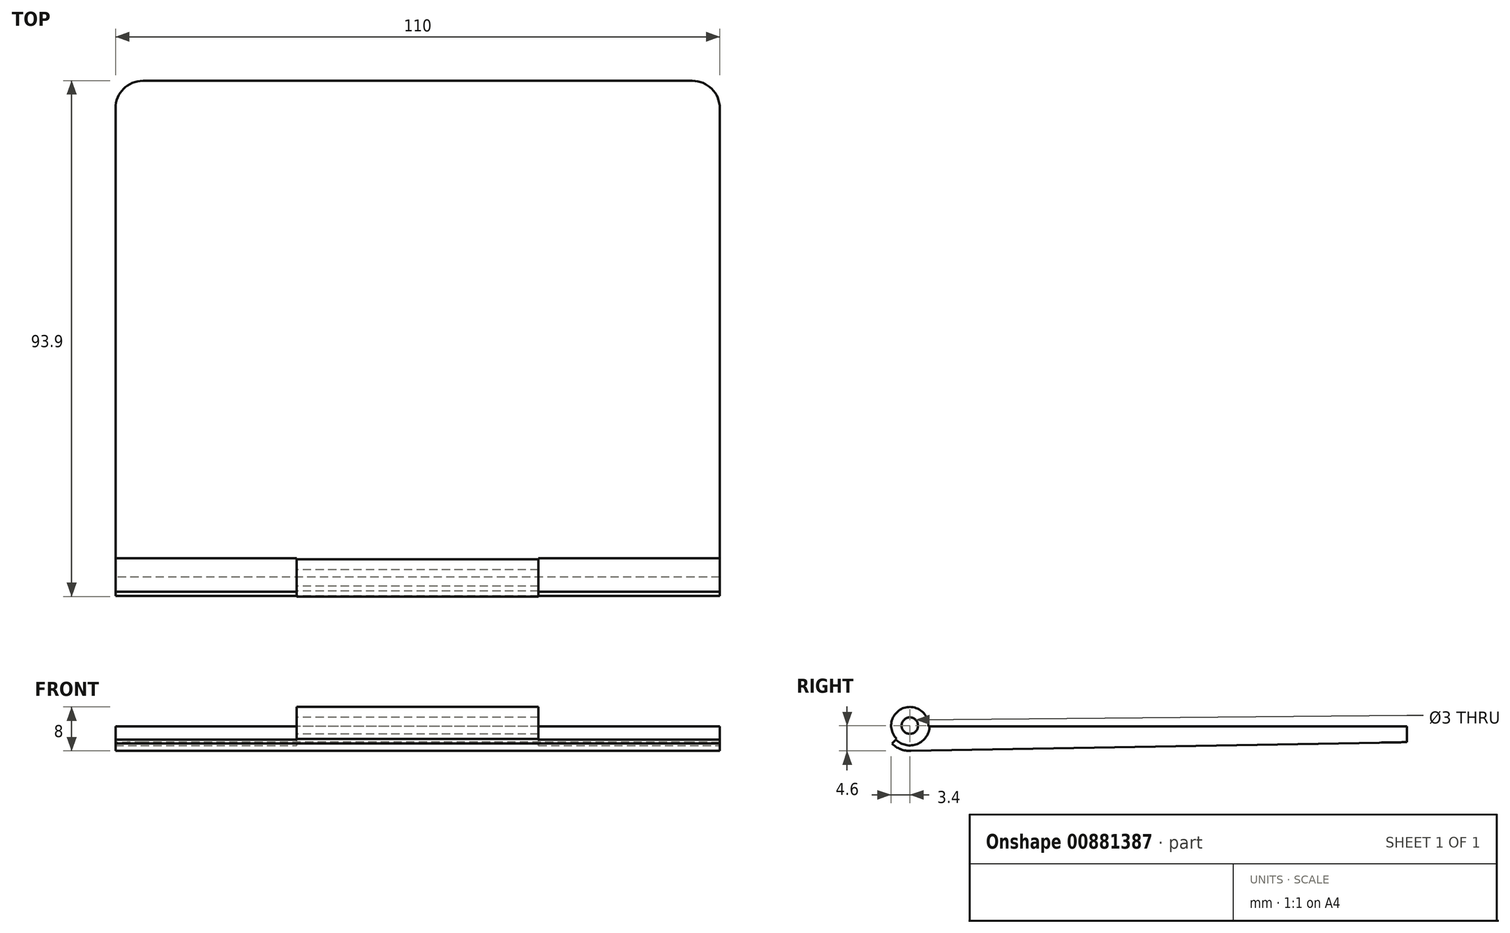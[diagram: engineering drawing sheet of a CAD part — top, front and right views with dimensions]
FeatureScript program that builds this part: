
annotation { "Feature Type Name" : "Feature", "Feature Type Description" : "" }
export const myFeature = defineFeature(function(context is Context, id is Id, definition is map)
    precondition{}
    {
        {
            var Q0;
            Q0=qCreatedBy(makeId("Top.planeOp"),FACE);
            var sketch = newSketch(context, id + "F0", { "sketchPlane" : qUnion([Q0])});
            skLineSegment(sketch, "E0.bottom", {"start": v(55, -45) * mm, "end": v(-55, -45) * mm});
            skLineSegment(sketch, "E0.top", {"start": v(55, 45) * mm, "end": v(-55, 45) * mm});
            skLineSegment(sketch, "E0.left", {"start": v(55, -45) * mm, "end": v(55, 45) * mm});
            skLineSegment(sketch, "E0.right", {"start": v(-55, -45) * mm, "end": v(-55, 45) * mm});
            skPoint(sketch, "E0.middle", {"position": v(0, 0) * mm});
            skLineSegment(sketch, "E1.bottom", {"start": v(52, 42) * mm, "end": v(-52, 42) * mm, "construction": true});
            skLineSegment(sketch, "E1.top", {"start": v(52, -42) * mm, "end": v(-52, -42) * mm, "construction": true});
            skLineSegment(sketch, "E1.left", {"start": v(52, 42) * mm, "end": v(52, -42) * mm, "construction": true});
            skLineSegment(sketch, "E1.right", {"start": v(-52, 42) * mm, "end": v(-52, -42) * mm, "construction": true});
            skSolve(sketch);
        }
        {
            var Q0;
            Q0=makeQuery(id+"F0.imprint","IMPRINT",FACE,{"disambiguationData":[TD([[makeQuery(id+"F0.imprint","IMPRINT",EDGE,{"derivedFrom":sQuery(id+"F0.wireOp",EDGE,"E0.bottom")}),-1.0]])]});
            extrude(context, id + "F1", {"entities" : qUnion([Q0]), "depth" : 3 * mm, "offsetDistance" : 25 * mm});
        }
        {
            var Q0;
            Q0=qCreatedBy(makeId("Right.planeOp"),FACE);
            var sketch = newSketch(context, id + "F2", { "sketchPlane" : qUnion([Q0])});
            skLineSegment(sketch, "E2", {"start": v(-42, 6.82) * mm, "end": v(-42, -5.48) * mm, "construction": true});
            skCircle(sketch, "E3", {"center": v(-45.5, 3) * mm, "radius": 1.5 * mm});
            skCircle(sketch, "E4", {"center": v(-45.5, 3) * mm, "radius": 3.4 * mm});
            skPoint(sketch, "E5", {"position": v(-42.1, 3) * mm});
            skPoint(sketch, "E6", {"position": v(-45.5, -0.4) * mm});
            skLineSegment(sketch, "E7", {"start": v(-48.55, 3) * mm, "end": v(-31.88, 3) * mm, "construction": true});
            skPoint(sketch, "E8", {"position": v(-42, 3) * mm});
            skCircle(sketch, "E9", {"center": v(-45.5, 3) * mm, "radius": 3.6 * mm});
            skLineSegment(sketch, "E10", {"start": v(-45.5, 3) * mm, "end": v(-49.84, -1.34) * mm, "construction": true});
            skPoint(sketch, "E11", {"position": v(-48.05, 0.45) * mm});
            skArc(sketch, "E12", {"start": v(-48.75, -0.25) * mm, "mid": v(-45.32, -1.6) * mm, "end": v(-42, 0.02) * mm});
            skPoint(sketch, "E13", {"position": v(-48.75, -0.25) * mm});
            skPoint(sketch, "E14", {"position": v(-42, 0.02) * mm});
            skLineSegment(sketch, "E15", {"start": v(-48.75, -0.25) * mm, "end": v(-48.05, 0.45) * mm});
            skPoint(sketch, "E16", {"position": v(-43.51, 0) * mm});
            skLineSegment(sketch, "E17", {"start": v(-42, 0.02) * mm, "end": v(-43.51, 0) * mm});
            skLineSegment(sketch, "E18", {"start": v(-42.1, 3) * mm, "end": v(-41.9, 3) * mm});
            skLineSegment(sketch, "E19", {"start": v(-48.05, 0.45) * mm, "end": v(-47.9, 0.6) * mm});
            skLineSegment(sketch, "E20", {"start": v(-43.51, 0) * mm, "end": v(-43.9, 0) * mm});
            skSolve(sketch);
        }
        {
            var Q0;
            Q0=makeQuery(id+"F2.imprint","IMPRINT",FACE,{"disambiguationData":[TD([[makeQuery(id+"F2.imprint","IMPRINT",EDGE,{"derivedFrom":sQuery(id+"F2.wireOp",EDGE,"E3")}),-1.0]])]});
            var Q1;
            Q1=makeQuery(id+"F2.imprint","IMPRINT",FACE,{"disambiguationData":[TD([[makeQuery(id+"F2.imprint","IMPRINT",EDGE,{"derivedFrom":sQuery(id+"F2.wireOp",EDGE,"E4")}),-1.0]])]});
            var Q2;
            Q2=makeQuery(id+"F2.imprint","IMPRINT",FACE,{"disambiguationData":[TD([[makeQuery(id+"F2.imprint","IMPRINT",EDGE,{"derivedFrom":sQuery(id+"F2.wireOp",EDGE,"E3")}),1.0]])]});
            var Q3;
            Q3=makeQuery(id+"F1.opExtrude","SWEPT_FACE",FACE,{"disambiguationData":[OSD([sQuery(id+"F0.wireOp",EDGE,"E0.right")])]});
            var Q4;
            Q4=makeQuery(id+"F1.opExtrude","SWEPT_FACE",FACE,{"disambiguationData":[OSD([sQuery(id+"F0.wireOp",EDGE,"E0.left")])]});
            extrude(context, id + "F3", {"entities" : qUnion([Q0, Q1, Q2]), "operationType" : NewBodyOperationType.REMOVE, "endBound" : BoundingType.UP_TO_SURFACE, "oppositeDirection" : true, "depth" : 25 * mm, "endBoundEntityFace" : qUnion([Q3]), "offsetDistance" : 25 * mm, "hasSecondDirection" : true, "secondDirectionBound" : SecondDirectionBoundingType.UP_TO_SURFACE, "secondDirectionOppositeDirection" : false, "secondDirectionDepth" : 25 * mm, "secondDirectionBoundEntityFace" : qUnion([Q4])});
        }
        {
            var Q0;
            {var subQ0=sQuery(id+"F2.wireOp",EDGE,"E18");Q0=makeQuery(id+"F2.imprint","IMPRINT",FACE,{"disambiguationData":[TD([[makeQuery(id+"F2.imprint","IMPRINT",EDGE,{"derivedFrom":subQ0}),-1.0]])]});}
            var Q1;
            {var subQ0=sQuery(id+"F2.wireOp",EDGE,"E19");Q1=makeQuery(id+"F2.imprint","IMPRINT",FACE,{"disambiguationData":[TD([[makeQuery(id+"F2.imprint","IMPRINT",EDGE,{"derivedFrom":subQ0}),-1.0]])]});}
            var Q2;
            Q2=makeQuery(id+"F2.imprint","IMPRINT",FACE,{"disambiguationData":[TD([[makeQuery(id+"F2.imprint","IMPRINT",EDGE,{"derivedFrom":sQuery(id+"F2.wireOp",EDGE,"E3")}),-1.0]])]});
            extrude(context, id + "F4", {"entities" : qUnion([Q0, Q1, Q2]), "operationType" : NewBodyOperationType.ADD, "depth" : 22 * mm, "offsetDistance" : 25 * mm, "hasSecondDirection" : true, "secondDirectionOppositeDirection" : true, "secondDirectionDepth" : 22 * mm});
        }
        {
            var Q0;
            Q0=makeQuery(id+"F2.imprint","IMPRINT",FACE,{"disambiguationData":[TD([[makeQuery(id+"F2.imprint","IMPRINT",EDGE,{"derivedFrom":sQuery(id+"F2.wireOp",EDGE,"E12")}),1.0]])]});
            var Q1;
            Q1=makeQuery(id+"F1.opExtrude","SWEPT_FACE",FACE,{"disambiguationData":[OSD([sQuery(id+"F0.wireOp",EDGE,"E0.left")])]});
            var Q2;
            Q2=makeQuery(id+"F1.opExtrude","SWEPT_FACE",FACE,{"disambiguationData":[OSD([sQuery(id+"F0.wireOp",EDGE,"E0.right")])]});
            extrude(context, id + "F5", {"entities" : qUnion([Q0]), "operationType" : NewBodyOperationType.ADD, "endBound" : BoundingType.UP_TO_SURFACE, "depth" : 25 * mm, "endBoundEntityFace" : qUnion([Q1]), "offsetDistance" : 25 * mm, "hasSecondDirection" : true, "secondDirectionBound" : SecondDirectionBoundingType.UP_TO_SURFACE, "secondDirectionOppositeDirection" : true, "secondDirectionDepth" : 25 * mm, "secondDirectionBoundEntityFace" : qUnion([Q2])});
        }
        {
            var Q0;
            Q0=makeQuery(id+"F4.boolean.opBoolean","MERGE",FACE,{"derivedFrom":[makeQuery(id+"F1.opExtrude","CAP_FACE",FACE,{"disambiguationData":[OSD([sQuery(id+"F0.wireOp",EDGE,"E0.bottom"),sQuery(id+"F0.wireOp",EDGE,"E0.top"),sQuery(id+"F0.wireOp",EDGE,"E0.left"),sQuery(id+"F0.wireOp",EDGE,"E0.right")])],"isStart":false}),makeQuery(id+"F4.opExtrude","SWEPT_FACE",FACE,{"disambiguationData":[OSD([sQuery(id+"F2.wireOp",EDGE,"E18")])]})]});
            var sketch = newSketch(context, id + "F6", { "sketchPlane" : qUnion([Q0])});
            skLineSegment(sketch, "E21.bottom", {"start": v(-55, 45) * mm, "end": v(55, 45) * mm});
            skLineSegment(sketch, "E21.top", {"start": v(-55, -41.9) * mm, "end": v(-22, -41.9) * mm});
            skLineSegment(sketch, "E21.left", {"start": v(-55, 45) * mm, "end": v(-55, -41.9) * mm});
            skLineSegment(sketch, "E21.right", {"start": v(55, 45) * mm, "end": v(55, -41.9) * mm});
            skLineSegment(sketch, "E22.bottom", {"start": v(-22, -42.1) * mm, "end": v(22, -42.1) * mm});
            skLineSegment(sketch, "E22.left", {"start": v(-22, -42.1) * mm, "end": v(-22, -41.9) * mm});
            skLineSegment(sketch, "E22.right", {"start": v(22, -42.1) * mm, "end": v(22, -41.9) * mm});
            skLineSegment(sketch, "E23.trimOffspring", {"start": v(22, -41.9) * mm, "end": v(55, -41.9) * mm});
            skSolve(sketch);
        }
        {
            var Q0;
            Q0=makeQuery(id+"F6.imprint","IMPRINT",FACE,{"disambiguationData":[TD([[makeQuery(id+"F6.imprint","IMPRINT",EDGE,{"derivedFrom":sQuery(id+"F6.wireOp",EDGE,"E21.bottom")}),1.0]])]});
            extrude(context, id + "F7", {"entities" : qUnion([Q0]), "operationType" : NewBodyOperationType.REMOVE, "oppositeDirection" : true, "depth" : 0.1 * mm, "offsetDistance" : 25 * mm});
        }
        {
            var Q0;
            Q0=makeQuery(id+"F5.boolean.opBoolean","MERGE",FACE,{"derivedFrom":[makeQuery(id+"F1.opExtrude","SWEPT_FACE",FACE,{"disambiguationData":[OSD([sQuery(id+"F0.wireOp",EDGE,"E0.right")])]}),makeQuery(id+"F5.opExtrude","CAP_FACE",FACE,{"disambiguationData":[OSD([sQuery(id+"F2.wireOp",EDGE,"E9"),sQuery(id+"F2.wireOp",EDGE,"E12"),sQuery(id+"F2.wireOp",EDGE,"E15"),sQuery(id+"F2.wireOp",EDGE,"E17")])],"isStart":true})]});
            var sketch = newSketch(context, id + "F8", { "sketchPlane" : qUnion([Q0])});
            skPoint(sketch, "E24.endSnap0", {"position": v(45.33, -1.6) * mm});
            skArc(sketch, "E25", {"start": v(42.01, 0) * mm, "mid": v(43.5, -1.14) * mm, "end": v(45.33, -1.6) * mm});
            skLineSegment(sketch, "E26", {"start": v(45.33, -1.6) * mm, "end": v(-45, 0) * mm});
            skLineSegment(sketch, "E27", {"start": v(-45, 0) * mm, "end": v(42.01, 0) * mm});
            skSolve(sketch);
        }
        {
            var Q0;
            Q0=makeQuery(id+"F8.imprint","IMPRINT",FACE,{"disambiguationData":[TD([[makeQuery(id+"F8.imprint","IMPRINT",EDGE,{"derivedFrom":sQuery(id+"F8.wireOp",EDGE,"E25")}),-1.0]])]});
            var Q1;
            Q1=makeQuery(id+"F5.boolean.opBoolean","MERGE",FACE,{"derivedFrom":[makeQuery(id+"F1.opExtrude","SWEPT_FACE",FACE,{"disambiguationData":[OSD([sQuery(id+"F0.wireOp",EDGE,"E0.left")])]}),makeQuery(id+"F5.opExtrude","CAP_FACE",FACE,{"disambiguationData":[OSD([sQuery(id+"F2.wireOp",EDGE,"E9"),sQuery(id+"F2.wireOp",EDGE,"E12"),sQuery(id+"F2.wireOp",EDGE,"E15"),sQuery(id+"F2.wireOp",EDGE,"E17")])],"isStart":false})]});
            extrude(context, id + "F9", {"entities" : qUnion([Q0]), "operationType" : NewBodyOperationType.ADD, "endBound" : BoundingType.UP_TO_SURFACE, "oppositeDirection" : true, "depth" : 25 * mm, "endBoundEntityFace" : qUnion([Q1]), "offsetDistance" : 25 * mm});
        }
        {
            var Q0;
            Q0=makeQuery(id+"F1.opExtrude","SWEPT_EDGE",EDGE,{"disambiguationData":[OSD([sQuery(id+"F0.wireOp",EDGE,"E0.top"),sQuery(id+"F0.wireOp",EDGE,"E0.right")])]});
            var Q1;
            Q1=makeQuery(id+"F1.opExtrude","SWEPT_EDGE",EDGE,{"disambiguationData":[OSD([sQuery(id+"F0.wireOp",EDGE,"E0.top"),sQuery(id+"F0.wireOp",EDGE,"E0.left")])]});
            fillet(context, id + "F10", {"entities" : qUnion([Q0, Q1]), "radius" : 5 * mm, "tangentPropagation" : true, "allowEdgeOverflow" : false});
        }
    });
